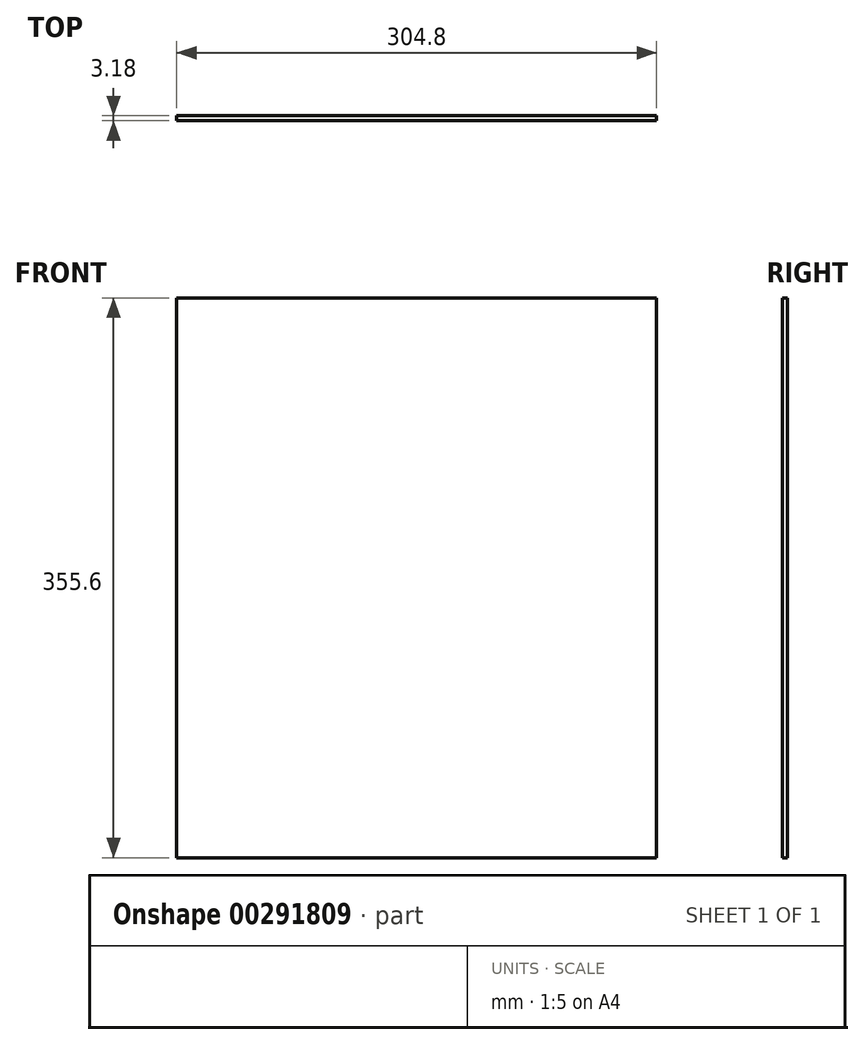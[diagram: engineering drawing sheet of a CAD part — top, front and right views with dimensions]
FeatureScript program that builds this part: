
annotation { "Feature Type Name" : "Feature", "Feature Type Description" : "" }
export const myFeature = defineFeature(function(context is Context, id is Id, definition is map)
    precondition{}
    {
        {
            var Q0;
            Q0=qCreatedBy(makeId("Front.planeOp"),FACE);
            var sketch = newSketch(context, id + "F0", { "sketchPlane" : qUnion([Q0])});
            skLineSegment(sketch, "E0.bottom", {"start": v(152.4, 177.8) * mm, "end": v(-152.4, 177.8) * mm});
            skLineSegment(sketch, "E0.top", {"start": v(152.4, -177.8) * mm, "end": v(-152.4, -177.8) * mm});
            skLineSegment(sketch, "E0.left", {"start": v(152.4, 177.8) * mm, "end": v(152.4, -177.8) * mm});
            skLineSegment(sketch, "E0.right", {"start": v(-152.4, 177.8) * mm, "end": v(-152.4, -177.8) * mm});
            skPoint(sketch, "E0.middle", {"position": v(0, 0) * mm});
            skSolve(sketch);
        }
        {
            var Q0;
            Q0 = qSketchRegion(id + "F0", true);
            extrude(context, id + "F1", {"entities" : qUnion([Q0]), "endBound" : BoundingType.SYMMETRIC, "depth" : 3.17 * mm});
        }
    });
